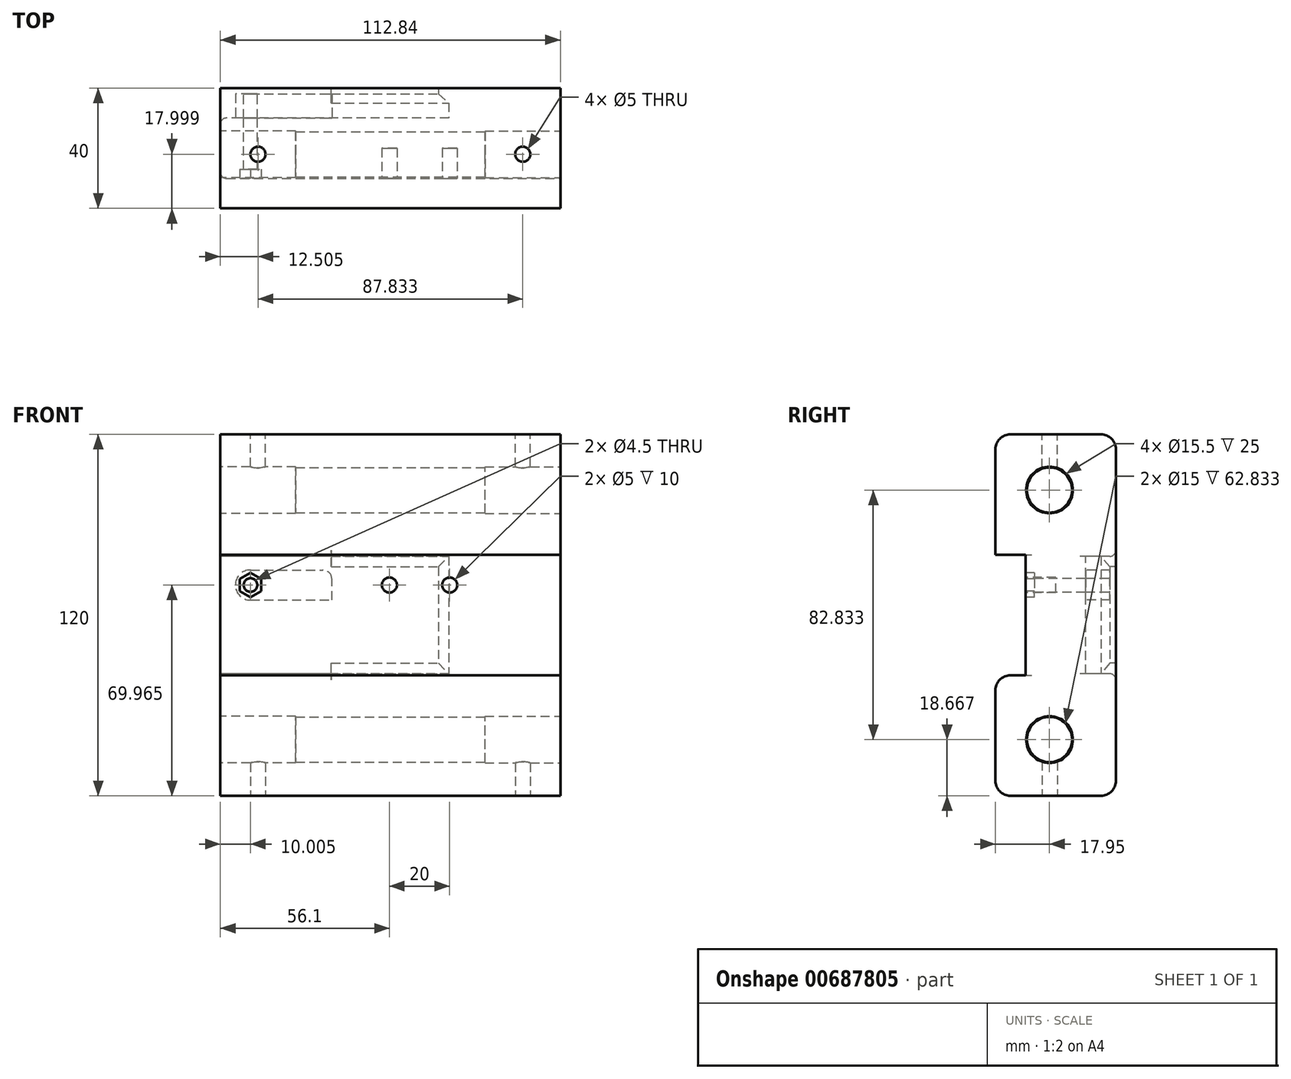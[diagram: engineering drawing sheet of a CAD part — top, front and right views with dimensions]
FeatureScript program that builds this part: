
annotation { "Feature Type Name" : "Feature", "Feature Type Description" : "" }
export const myFeature = defineFeature(function(context is Context, id is Id, definition is map)
    precondition{}
    {
        {
            var Q0;
            Q0=qCreatedBy(makeId("Top.planeOp"),FACE);
            var sketch = newSketch(context, id + "F0", { "sketchPlane" : qUnion([Q0])});
            skLineSegment(sketch, "E0.bottom", {"start": v(-54.1, 12.05) * mm, "end": v(58.73, 12.05) * mm});
            skLineSegment(sketch, "E0.top", {"start": v(-54.1, -17.95) * mm, "end": v(58.73, -17.95) * mm});
            skLineSegment(sketch, "E0.left", {"start": v(-54.1, 12.05) * mm, "end": v(-54.1, -17.95) * mm});
            skLineSegment(sketch, "E0.right", {"start": v(58.73, 12.05) * mm, "end": v(58.73, -17.95) * mm});
            skSolve(sketch);
        }
        {
            var Q0;
            Q0=makeQuery(id+"F0.imprint","IMPRINT",FACE,{"disambiguationData":[TD([[makeQuery(id+"F0.imprint","IMPRINT",EDGE,{"derivedFrom":sQuery(id+"F0.wireOp",EDGE,"E0.bottom")}),-1.0]])]});
            extrude(context, id + "F1", {"entities" : qUnion([Q0]), "depth" : 120 * mm, "offsetDistance" : 25 * mm});
        }
        {
            var Q0;
            Q0=makeQuery(id+"F1.opExtrude","SWEPT_FACE",FACE,{"disambiguationData":[OSD([sQuery(id+"F0.wireOp",EDGE,"E0.bottom")])]});
            var sketch = newSketch(context, id + "F2", { "sketchPlane" : qUnion([Q0])});
            skLineSegment(sketch, "E1.bottom", {"start": v(-21.73, 40.5) * mm, "end": v(17.27, 40.5) * mm});
            skLineSegment(sketch, "E1.top", {"start": v(-21.73, 79.5) * mm, "end": v(17.27, 79.5) * mm});
            skLineSegment(sketch, "E1.left", {"start": v(-21.73, 40.5) * mm, "end": v(-21.73, 79.5) * mm});
            skLineSegment(sketch, "E2.bottom", {"start": v(-18.73, 43.5) * mm, "end": v(14.27, 43.5) * mm});
            skLineSegment(sketch, "E2.top", {"start": v(-18.73, 76.5) * mm, "end": v(14.27, 76.5) * mm});
            skLineSegment(sketch, "E2.left", {"start": v(-18.73, 43.5) * mm, "end": v(-18.73, 76.5) * mm});
            skLineSegment(sketch, "E3.bottom", {"start": v(17.27, 40.5) * mm, "end": v(54.1, 40.5) * mm});
            skLineSegment(sketch, "E3.top", {"start": v(17.27, 79.5) * mm, "end": v(54.1, 79.5) * mm});
            skLineSegment(sketch, "E3.right", {"start": v(54.1, 40.5) * mm, "end": v(54.1, 79.5) * mm});
            skSolve(sketch);
        }
        {
            var Q0;
            Q0=makeQuery(id+"F2.imprint","IMPRINT",FACE,{"disambiguationData":[TD([[makeQuery(id+"F2.imprint","IMPRINT",EDGE,{"derivedFrom":sQuery(id+"F2.wireOp",EDGE,"E1.bottom")}),-1.0]])]});
            extrude(context, id + "F3", {"entities" : qUnion([Q0]), "operationType" : NewBodyOperationType.ADD, "depth" : 10 * mm, "offsetDistance" : 25 * mm});
        }
        {
            var Q0;
            Q0=makeQuery(id+"F3.opExtrude","SWEPT_FACE",FACE,{"disambiguationData":[OSD([sQuery(id+"F2.wireOp",EDGE,"E1.bottom"),sQuery(id+"F2.wireOp",EDGE,"E3.bottom")])]});
            var sketch = newSketch(context, id + "F4", { "sketchPlane" : qUnion([Q0])});
            skLineSegment(sketch, "E4", {"start": v(18.23, 22.05) * mm, "end": v(18.23, 20.05) * mm});
            skLineSegment(sketch, "E5", {"start": v(18.23, 20.05) * mm, "end": v(21.73, 17.05) * mm});
            skLineSegment(sketch, "E6", {"start": v(21.73, 17.05) * mm, "end": v(21.73, 22.05) * mm});
            skLineSegment(sketch, "E7", {"start": v(21.73, 22.05) * mm, "end": v(18.23, 22.05) * mm});
            skSolve(sketch);
        }
        {
            var Q0;
            Q0=makeQuery(id+"F3.opExtrude","SWEPT_FACE",FACE,{"disambiguationData":[OSD([sQuery(id+"F2.wireOp",EDGE,"E1.left")])]});
            var sketch = newSketch(context, id + "F5", { "sketchPlane" : qUnion([Q0])});
            skLineSegment(sketch, "E8", {"start": v(-17.05, 40.5) * mm, "end": v(-20.05, 44) * mm});
            skLineSegment(sketch, "E9", {"start": v(-20.05, 44) * mm, "end": v(-22.05, 44) * mm});
            skLineSegment(sketch, "E10", {"start": v(-22.05, 44) * mm, "end": v(-22.05, 40.5) * mm});
            skLineSegment(sketch, "E11", {"start": v(-22.05, 40.5) * mm, "end": v(-17.05, 40.5) * mm});
            skLineSegment(sketch, "E12", {"start": v(-22.05, 60) * mm, "end": v(-12.05, 60) * mm, "construction": true});
            skLineSegment(sketch, "E13.MirrorCS", {"start": v(-17.05, 79.5) * mm, "end": v(-20.05, 76) * mm});
            skLineSegment(sketch, "E14.MirrorCS", {"start": v(-22.05, 79.5) * mm, "end": v(-17.05, 79.5) * mm});
            skLineSegment(sketch, "E15.MirrorCS", {"start": v(-20.05, 76) * mm, "end": v(-22.05, 76) * mm});
            skLineSegment(sketch, "E16.MirrorCS", {"start": v(-22.05, 76) * mm, "end": v(-22.05, 79.5) * mm});
            skSolve(sketch);
        }
        {
            var Q0;
            Q0=makeQuery(id+"F5.imprint","IMPRINT",FACE,{"disambiguationData":[TD([[makeQuery(id+"F5.imprint","IMPRINT",EDGE,{"derivedFrom":sQuery(id+"F5.wireOp",EDGE,"E8")}),1.0]])]});
            var Q1;
            Q1=makeQuery(id+"F5.imprint","IMPRINT",FACE,{"disambiguationData":[TD([[makeQuery(id+"F5.imprint","IMPRINT",EDGE,{"derivedFrom":sQuery(id+"F5.wireOp",EDGE,"E13.MirrorCS")}),-1.0]])]});
            extrude(context, id + "F6", {"entities" : qUnion([Q0, Q1]), "operationType" : NewBodyOperationType.ADD, "depth" : 39 * mm, "offsetDistance" : 25 * mm});
        }
        {
            var Q0;
            Q0=makeQuery(id+"F4.imprint","IMPRINT",FACE,{"disambiguationData":[TD([[makeQuery(id+"F4.imprint","IMPRINT",EDGE,{"derivedFrom":sQuery(id+"F4.wireOp",EDGE,"E4")}),1.0]])]});
            extrude(context, id + "F7", {"entities" : qUnion([Q0]), "operationType" : NewBodyOperationType.ADD, "depth" : 39 * mm, "offsetDistance" : 25 * mm});
        }
        {
            var Q0;
            {var subQ0=sQuery(id+"F0.wireOp",EDGE,"E0.right");Q0=makeQuery(id+"F3.boolean.opBoolean","MERGE",FACE,{"derivedFrom":[makeQuery(id+"F1.opExtrude","SWEPT_FACE",FACE,{"disambiguationData":[OSD([subQ0])]}),makeQuery(id+"F3.opExtrude","SWEPT_FACE",FACE,{"disambiguationData":[OSD([sQuery(id+"F0.wireOp",EDGE,"E0.bottom"),subQ0])]})]});}
            var sketch = newSketch(context, id + "F8", { "sketchPlane" : qUnion([Q0])});
            skCircle(sketch, "E17", {"center": v(0, 101.5) * mm, "radius": 7.5 * mm});
            skCircle(sketch, "E18", {"center": v(0, 18.67) * mm, "radius": 7.5 * mm});
            skLineSegment(sketch, "E19.bottom", {"start": v(-17.95, 40) * mm, "end": v(-7.95, 40) * mm});
            skLineSegment(sketch, "E19.top", {"start": v(-17.95, 80) * mm, "end": v(-7.95, 80) * mm});
            skLineSegment(sketch, "E19.left", {"start": v(-17.95, 40) * mm, "end": v(-17.95, 80) * mm});
            skLineSegment(sketch, "E19.right", {"start": v(-7.95, 40) * mm, "end": v(-7.95, 80) * mm});
            skSolve(sketch);
        }
        {
            var Q0;
            Q0=makeQuery(id+"F8.imprint","IMPRINT",FACE,{"disambiguationData":[TD([[makeQuery(id+"F8.imprint","IMPRINT",EDGE,{"derivedFrom":sQuery(id+"F8.wireOp",EDGE,"E17")}),1.0]])]});
            var Q1;
            Q1=makeQuery(id+"F8.imprint","IMPRINT",FACE,{"disambiguationData":[TD([[makeQuery(id+"F8.imprint","IMPRINT",EDGE,{"derivedFrom":sQuery(id+"F8.wireOp",EDGE,"E18")}),1.0]])]});
            var Q2;
            Q2=makeQuery(id+"F8.imprint","IMPRINT",FACE,{"disambiguationData":[TD([[makeQuery(id+"F8.imprint","IMPRINT",EDGE,{"derivedFrom":sQuery(id+"F8.wireOp",EDGE,"E19.bottom")}),1.0]])]});
            extrude(context, id + "F9", {"entities" : qUnion([Q0, Q1, Q2]), "operationType" : NewBodyOperationType.REMOVE, "oppositeDirection" : true, "depth" : 120 * mm, "offsetDistance" : 25 * mm});
        }
        {
            var Q0;
            Q0=makeQuery(id+"F1.opExtrude","SWEPT_FACE",FACE,{"disambiguationData":[OSD([sQuery(id+"F0.wireOp",EDGE,"E0.bottom")])]});
            var sketch = newSketch(context, id + "F10", { "sketchPlane" : qUnion([Q0])});
            skArc(sketch, "E20", {"start": v(44.1, 64.96) * mm, "mid": v(49.1, 69.96) * mm, "end": v(44.1, 74.96) * mm});
            skLineSegment(sketch, "E21.bottom", {"start": v(44.1, 64.96) * mm, "end": v(17.1, 64.96) * mm});
            skLineSegment(sketch, "E21.top", {"start": v(44.1, 74.96) * mm, "end": v(20.1, 74.96) * mm});
            skLineSegment(sketch, "E21.right", {"start": v(17.1, 64.96) * mm, "end": v(17.1, 71.96) * mm});
            skPoint(sketch, "E22.visualSharp", {"position": v(17.1, 74.96) * mm});
            skArc(sketch, "E22.filletArc", {"start": v(20.1, 74.96) * mm, "mid": v(17.98, 74.09) * mm, "end": v(17.1, 71.96) * mm});
            skSolve(sketch);
        }
        {
            var Q0;
            Q0=makeQuery(id+"F10.imprint","IMPRINT",FACE,{"disambiguationData":[TD([[makeQuery(id+"F10.imprint","IMPRINT",EDGE,{"derivedFrom":sQuery(id+"F10.wireOp",EDGE,"E20")}),1.0]])]});
            extrude(context, id + "F11", {"entities" : qUnion([Q0]), "depth" : 8 * mm, "offsetDistance" : 25 * mm});
        }
        {
            var Q0;
            Q0=makeQuery(id+"F11.opExtrude","CAP_FACE",FACE,{"disambiguationData":[OSD([sQuery(id+"F10.wireOp",EDGE,"E20"),sQuery(id+"F10.wireOp",EDGE,"E21.bottom"),sQuery(id+"F10.wireOp",EDGE,"E21.top"),sQuery(id+"F10.wireOp",EDGE,"E21.right"),sQuery(id+"F10.wireOp",EDGE,"E22.filletArc")])],"isStart":false});
            var sketch = newSketch(context, id + "F12", { "sketchPlane" : qUnion([Q0])});
            skCircle(sketch, "E23", {"center": v(44.1, 69.96) * mm, "radius": 2.25 * mm});
            skSolve(sketch);
        }
        {
            var Q0;
            Q0=makeQuery(id+"F12.imprint","IMPRINT",FACE,{"disambiguationData":[TD([[makeQuery(id+"F12.imprint","IMPRINT",EDGE,{"derivedFrom":sQuery(id+"F12.wireOp",EDGE,"E23")}),1.0]])]});
            extrude(context, id + "F13", {"entities" : qUnion([Q0]), "operationType" : NewBodyOperationType.REMOVE, "oppositeDirection" : true, "depth" : 50 * mm, "offsetDistance" : 25 * mm});
        }
        {
            var Q0;
            Q0=makeQuery(id+"F9.boolean.opBoolean","COPY",FACE,{"derivedFrom":makeQuery(id+"F9.opExtrude","SWEPT_FACE",FACE,{"disambiguationData":[OSD([sQuery(id+"F8.wireOp",EDGE,"E19.right")])]})});
            var sketch = newSketch(context, id + "F14", { "sketchPlane" : qUnion([Q0])});
            skCircle(sketch, "E24.cCircle", {"center": v(-44.1, 69.96) * mm, "radius": 3.5 * mm, "construction": true});
            skLineSegment(sketch, "E24.0", {"start": v(-40.6, 71.99) * mm, "end": v(-40.6, 67.94) * mm});
            skLineSegment(sketch, "E24.1", {"start": v(-40.6, 67.94) * mm, "end": v(-44.1, 65.92) * mm});
            skLineSegment(sketch, "E24.2", {"start": v(-44.1, 65.92) * mm, "end": v(-47.6, 67.94) * mm});
            skLineSegment(sketch, "E24.3", {"start": v(-47.6, 67.94) * mm, "end": v(-47.6, 71.99) * mm});
            skLineSegment(sketch, "E24.4", {"start": v(-47.6, 71.99) * mm, "end": v(-44.1, 74) * mm});
            skLineSegment(sketch, "E24.5", {"start": v(-44.1, 74) * mm, "end": v(-40.6, 71.99) * mm});
            skPoint(sketch, "E24.0.midPoint", {"position": v(-40.6, 69.96) * mm});
            skCircle(sketch, "E25", {"center": v(1.99, 69.96) * mm, "radius": 2.5 * mm});
            skCircle(sketch, "E26", {"center": v(21.99, 69.96) * mm, "radius": 2.5 * mm});
            skSolve(sketch);
        }
        {
            var Q0;
            Q0=makeQuery(id+"F14.imprint","IMPRINT",FACE,{"disambiguationData":[TD([[makeQuery(id+"F14.imprint","IMPRINT",EDGE,{"derivedFrom":sQuery(id+"F14.wireOp",EDGE,"E24.0")}),-1.0]])]});
            extrude(context, id + "F15", {"entities" : qUnion([Q0]), "operationType" : NewBodyOperationType.REMOVE, "oppositeDirection" : true, "depth" : 3 * mm, "offsetDistance" : 25 * mm});
        }
        {
            var Q0;
            Q0=makeQuery(id+"F9.boolean.opBoolean","COPY",EDGE,{"derivedFrom":makeQuery(id+"F9.opExtrude","SWEPT_EDGE",EDGE,{"disambiguationData":[OSD([sQuery(id+"F0.wireOp",EDGE,"E0.top"),sQuery(id+"F0.wireOp",EDGE,"E0.right"),sQuery(id+"F8.wireOp",EDGE,"E19.bottom"),sQuery(id+"F8.wireOp",EDGE,"E19.left")])]})});
            var Q1;
            Q1=makeQuery(id+"F9.boolean.opBoolean","COPY",EDGE,{"derivedFrom":makeQuery(id+"F9.opExtrude","SWEPT_EDGE",EDGE,{"disambiguationData":[OSD([sQuery(id+"F0.wireOp",EDGE,"E0.top"),sQuery(id+"F0.wireOp",EDGE,"E0.right"),sQuery(id+"F8.wireOp",EDGE,"E19.top"),sQuery(id+"F8.wireOp",EDGE,"E19.left")])]})});
            var Q2;
            Q2=makeQuery(id+"F1.opExtrude","CAP_EDGE",EDGE,{"disambiguationData":[OSD([sQuery(id+"F0.wireOp",EDGE,"E0.top")])],"isStart":false});
            var Q3;
            {var subQ0=sQuery(id+"F0.wireOp",EDGE,"E0.bottom");Q3=makeQuery(id+"F3.opExtrude","CAP_EDGE",EDGE,{"disambiguationData":[OSD([subQ0]),TDD([makeQuery(id+"F2.imprint","IMPRINT",EDGE,{"derivedFrom":makeQuery(id+"F1.opExtrude","CAP_EDGE",EDGE,{"disambiguationData":[OSD([subQ0])],"isStart":false})})])],"isStart":false});}
            var Q4;
            Q4=makeQuery(id+"F1.opExtrude","CAP_EDGE",EDGE,{"disambiguationData":[OSD([sQuery(id+"F0.wireOp",EDGE,"E0.top")])],"isStart":true});
            var Q5;
            {var subQ0=sQuery(id+"F0.wireOp",EDGE,"E0.bottom");Q5=makeQuery(id+"F3.opExtrude","CAP_EDGE",EDGE,{"disambiguationData":[OSD([subQ0]),TDD([makeQuery(id+"F2.imprint","IMPRINT",EDGE,{"derivedFrom":makeQuery(id+"F1.opExtrude","CAP_EDGE",EDGE,{"disambiguationData":[OSD([subQ0])],"isStart":true})})])],"isStart":false});}
            fillet(context, id + "F16", {"entities" : qUnion([Q0, Q1, Q2, Q3, Q4, Q5]), "radius" : 5 * mm, "tangentPropagation" : true, "allowEdgeOverflow" : false});
        }
        {
            var Q0;
            Q0=makeQuery(id+"F3.opExtrude","CAP_EDGE",EDGE,{"disambiguationData":[OSD([sQuery(id+"F2.wireOp",EDGE,"E1.top"),sQuery(id+"F2.wireOp",EDGE,"E3.top")])],"isStart":false});
            var Q1;
            Q1=makeQuery(id+"F3.opExtrude","CAP_EDGE",EDGE,{"disambiguationData":[OSD([sQuery(id+"F2.wireOp",EDGE,"E1.bottom"),sQuery(id+"F2.wireOp",EDGE,"E3.bottom")])],"isStart":false});
            var Q2;
            Q2=makeQuery(id+"F1.opExtrude","SWEPT_EDGE",EDGE,{"disambiguationData":[OSD([sQuery(id+"F0.wireOp",EDGE,"E0.bottom"),sQuery(id+"F0.wireOp",EDGE,"E0.left")])]});
            var Q3;
            {var subQ0=sQuery(id+"F0.wireOp",EDGE,"E0.bottom");var subQ1=sQuery(id+"F0.wireOp",EDGE,"E0.left");var subQ2=makeQuery(id+"F1.opExtrude","SWEPT_EDGE",EDGE,{"disambiguationData":[OSD([subQ0,subQ1])]});Q3=makeQuery(id+"F9.boolean.opBoolean","INTERSECT",EDGE,{"derivedFrom":[makeQuery(id+"F3.boolean.opBoolean","MERGE",FACE,{"derivedFrom":[makeQuery(id+"F1.opExtrude","SWEPT_FACE",FACE,{"disambiguationData":[OSD([subQ1])]}),makeQuery(id+"F3.opExtrude","SWEPT_FACE",FACE,{"disambiguationData":[OSD([subQ0,subQ1]),TDD([makeQuery(id+"F2.imprint","IMPRINT",EDGE,{"disambiguationData":[TD([[makeQuery(id+"F2.imprint","INTERSECT",VERTEX,{"derivedFrom":[subQ2,makeQuery(id+"F1.opExtrude","CAP_EDGE",EDGE,{"disambiguationData":[OSD([subQ0])],"isStart":true})]}),1.0]])],"derivedFrom":subQ2})])]}),makeQuery(id+"F3.opExtrude","SWEPT_FACE",FACE,{"disambiguationData":[OSD([subQ0,subQ1]),TDD([makeQuery(id+"F2.imprint","IMPRINT",EDGE,{"disambiguationData":[TD([[makeQuery(id+"F2.imprint","INTERSECT",VERTEX,{"derivedFrom":[subQ2,makeQuery(id+"F1.opExtrude","CAP_EDGE",EDGE,{"disambiguationData":[OSD([subQ0])],"isStart":false})]}),-1.0]])],"derivedFrom":subQ2})])]})]}),makeQuery(id+"F9.opExtrude","SWEPT_FACE",FACE,{"disambiguationData":[OSD([sQuery(id+"F8.wireOp",EDGE,"E19.right")])]})]});}
            var Q4;
            Q4=makeQuery(id+"F9.boolean.opBoolean","COPY",EDGE,{"derivedFrom":makeQuery(id+"F9.opExtrude","CAP_EDGE",EDGE,{"disambiguationData":[OSD([sQuery(id+"F8.wireOp",EDGE,"E19.right")])],"isStart":true})});
            fillet(context, id + "F17", {"entities" : qUnion([Q0, Q1, Q2, Q3, Q4]), "radius" : 2 * mm, "tangentPropagation" : true, "allowEdgeOverflow" : false});
        }
        {
            var Q0;
            Q0=makeQuery(id+"F14.imprint","IMPRINT",FACE,{"disambiguationData":[TD([[makeQuery(id+"F14.imprint","IMPRINT",EDGE,{"derivedFrom":sQuery(id+"F14.wireOp",EDGE,"E25")}),1.0]])]});
            var Q1;
            Q1=makeQuery(id+"F14.imprint","IMPRINT",FACE,{"disambiguationData":[TD([[makeQuery(id+"F14.imprint","IMPRINT",EDGE,{"derivedFrom":sQuery(id+"F14.wireOp",EDGE,"E26")}),1.0]])]});
            extrude(context, id + "F18", {"entities" : qUnion([Q0, Q1]), "operationType" : NewBodyOperationType.REMOVE, "oppositeDirection" : true, "depth" : 10 * mm, "offsetDistance" : 25 * mm});
        }
        {
            var Q0;
            {var subQ0=sQuery(id+"F0.wireOp",EDGE,"E0.right");Q0=makeQuery(id+"F3.boolean.opBoolean","MERGE",FACE,{"derivedFrom":[makeQuery(id+"F1.opExtrude","SWEPT_FACE",FACE,{"disambiguationData":[OSD([subQ0])]}),makeQuery(id+"F3.opExtrude","SWEPT_FACE",FACE,{"disambiguationData":[OSD([sQuery(id+"F0.wireOp",EDGE,"E0.bottom"),subQ0])]})]});}
            var sketch = newSketch(context, id + "F19", { "sketchPlane" : qUnion([Q0])});
            skCircle(sketch, "E27", {"center": v(0, 101.5) * mm, "radius": 7.75 * mm});
            skCircle(sketch, "E28", {"center": v(0, 18.67) * mm, "radius": 7.75 * mm});
            skSolve(sketch);
        }
        {
            var Q0;
            Q0=makeQuery(id+"F19.imprint","IMPRINT",FACE,{"disambiguationData":[TD([[makeQuery(id+"F19.imprint","IMPRINT",EDGE,{"derivedFrom":sQuery(id+"F19.wireOp",EDGE,"E27")}),1.0]])]});
            var Q1;
            Q1=makeQuery(id+"F19.imprint","IMPRINT",FACE,{"disambiguationData":[TD([[makeQuery(id+"F19.imprint","IMPRINT",EDGE,{"derivedFrom":sQuery(id+"F19.wireOp",EDGE,"E28")}),1.0]])]});
            extrude(context, id + "F20", {"entities" : qUnion([Q0, Q1]), "operationType" : NewBodyOperationType.REMOVE, "oppositeDirection" : true, "depth" : 25 * mm, "offsetDistance" : 25 * mm});
        }
        {
            var Q0;
            {var subQ0=sQuery(id+"F0.wireOp",EDGE,"E0.bottom");var subQ1=sQuery(id+"F0.wireOp",EDGE,"E0.left");var subQ2=makeQuery(id+"F1.opExtrude","SWEPT_EDGE",EDGE,{"disambiguationData":[OSD([subQ0,subQ1])]});Q0=makeQuery(id+"F3.boolean.opBoolean","MERGE",FACE,{"derivedFrom":[makeQuery(id+"F1.opExtrude","SWEPT_FACE",FACE,{"disambiguationData":[OSD([subQ1])]}),makeQuery(id+"F3.opExtrude","SWEPT_FACE",FACE,{"disambiguationData":[OSD([subQ0,subQ1]),TDD([makeQuery(id+"F2.imprint","IMPRINT",EDGE,{"disambiguationData":[TD([[makeQuery(id+"F2.imprint","INTERSECT",VERTEX,{"derivedFrom":[subQ2,makeQuery(id+"F1.opExtrude","CAP_EDGE",EDGE,{"disambiguationData":[OSD([subQ0])],"isStart":true})]}),1.0]])],"derivedFrom":subQ2})])]}),makeQuery(id+"F3.opExtrude","SWEPT_FACE",FACE,{"disambiguationData":[OSD([subQ0,subQ1]),TDD([makeQuery(id+"F2.imprint","IMPRINT",EDGE,{"disambiguationData":[TD([[makeQuery(id+"F2.imprint","INTERSECT",VERTEX,{"derivedFrom":[subQ2,makeQuery(id+"F1.opExtrude","CAP_EDGE",EDGE,{"disambiguationData":[OSD([subQ0])],"isStart":false})]}),-1.0]])],"derivedFrom":subQ2})])]})]});}
            var sketch = newSketch(context, id + "F21", { "sketchPlane" : qUnion([Q0])});
            skCircle(sketch, "E29", {"center": v(0, 101.5) * mm, "radius": 7.75 * mm});
            skCircle(sketch, "E30", {"center": v(0, 18.67) * mm, "radius": 7.75 * mm});
            skSolve(sketch);
        }
        {
            var Q0;
            Q0=makeQuery(id+"F21.imprint","IMPRINT",FACE,{"disambiguationData":[TD([[makeQuery(id+"F21.imprint","IMPRINT",EDGE,{"derivedFrom":sQuery(id+"F21.wireOp",EDGE,"E29")}),1.0]])]});
            var Q1;
            Q1=makeQuery(id+"F21.imprint","IMPRINT",FACE,{"disambiguationData":[TD([[makeQuery(id+"F21.imprint","IMPRINT",EDGE,{"derivedFrom":sQuery(id+"F21.wireOp",EDGE,"E30")}),1.0]])]});
            extrude(context, id + "F22", {"entities" : qUnion([Q0, Q1]), "operationType" : NewBodyOperationType.REMOVE, "oppositeDirection" : true, "depth" : 25 * mm, "offsetDistance" : 25 * mm});
        }
        {
            var Q0;
            {var subQ0=sQuery(id+"F0.wireOp",EDGE,"E0.bottom");Q0=makeQuery(id+"F3.boolean.opBoolean","MERGE",FACE,{"derivedFrom":[makeQuery(id+"F1.opExtrude","CAP_FACE",FACE,{"disambiguationData":[OSD([subQ0,sQuery(id+"F0.wireOp",EDGE,"E0.top"),sQuery(id+"F0.wireOp",EDGE,"E0.left"),sQuery(id+"F0.wireOp",EDGE,"E0.right")])],"isStart":true}),makeQuery(id+"F3.opExtrude","SWEPT_FACE",FACE,{"disambiguationData":[OSD([subQ0]),TDD([makeQuery(id+"F2.imprint","IMPRINT",EDGE,{"derivedFrom":makeQuery(id+"F1.opExtrude","CAP_EDGE",EDGE,{"disambiguationData":[OSD([subQ0])],"isStart":true})})])]})]});}
            var sketch = newSketch(context, id + "F23", { "sketchPlane" : qUnion([Q0])});
            skCircle(sketch, "E31", {"center": v(-41.6, -0.05) * mm, "radius": 2.5 * mm});
            skPoint(sketch, "E31.centerSnap0", {"position": v(-54.1, -0.05) * mm});
            skCircle(sketch, "E32", {"center": v(46.23, -0.05) * mm, "radius": 2.5 * mm});
            skPoint(sketch, "E32.centerSnap0", {"position": v(58.73, -0.05) * mm});
            skSolve(sketch);
        }
        {
            var Q0;
            {var subQ0=sQuery(id+"F0.wireOp",EDGE,"E0.bottom");Q0=makeQuery(id+"F3.boolean.opBoolean","MERGE",FACE,{"derivedFrom":[makeQuery(id+"F1.opExtrude","CAP_FACE",FACE,{"disambiguationData":[OSD([subQ0,sQuery(id+"F0.wireOp",EDGE,"E0.top"),sQuery(id+"F0.wireOp",EDGE,"E0.left"),sQuery(id+"F0.wireOp",EDGE,"E0.right")])],"isStart":false}),makeQuery(id+"F3.opExtrude","SWEPT_FACE",FACE,{"disambiguationData":[OSD([subQ0]),TDD([makeQuery(id+"F2.imprint","IMPRINT",EDGE,{"derivedFrom":makeQuery(id+"F1.opExtrude","CAP_EDGE",EDGE,{"disambiguationData":[OSD([subQ0])],"isStart":false})})])]})]});}
            var sketch = newSketch(context, id + "F24", { "sketchPlane" : qUnion([Q0])});
            skCircle(sketch, "E33", {"center": v(-41.6, 0.05) * mm, "radius": 2.5 * mm});
            skPoint(sketch, "E33.centerSnap0", {"position": v(-54.1, 0.05) * mm});
            skCircle(sketch, "E34", {"center": v(46.23, 0.05) * mm, "radius": 2.5 * mm});
            skPoint(sketch, "E34.centerSnap0", {"position": v(58.73, 0.05) * mm});
            skSolve(sketch);
        }
        {
            var Q0;
            Q0=makeQuery(id+"F24.imprint","IMPRINT",FACE,{"disambiguationData":[TD([[makeQuery(id+"F24.imprint","IMPRINT",EDGE,{"derivedFrom":sQuery(id+"F24.wireOp",EDGE,"E33")}),1.0]])]});
            var Q1;
            Q1=makeQuery(id+"F23.imprint","IMPRINT",FACE,{"disambiguationData":[TD([[makeQuery(id+"F23.imprint","IMPRINT",EDGE,{"derivedFrom":sQuery(id+"F23.wireOp",EDGE,"E31")}),1.0]])]});
            var Q2;
            Q2=makeQuery(id+"F24.imprint","IMPRINT",FACE,{"disambiguationData":[TD([[makeQuery(id+"F24.imprint","IMPRINT",EDGE,{"derivedFrom":sQuery(id+"F24.wireOp",EDGE,"E34")}),1.0]])]});
            var Q3;
            Q3=makeQuery(id+"F23.imprint","IMPRINT",FACE,{"disambiguationData":[TD([[makeQuery(id+"F23.imprint","IMPRINT",EDGE,{"derivedFrom":sQuery(id+"F23.wireOp",EDGE,"E32")}),1.0]])]});
            extrude(context, id + "F25", {"entities" : qUnion([Q0, Q1, Q2, Q3]), "operationType" : NewBodyOperationType.REMOVE, "oppositeDirection" : true, "depth" : 13.1 * mm, "offsetDistance" : 25 * mm});
        }
        {
            var Q0;
            Q0=makeQuery(id+"F23.imprint","IMPRINT",FACE,{"disambiguationData":[TD([[makeQuery(id+"F23.imprint","IMPRINT",EDGE,{"derivedFrom":sQuery(id+"F23.wireOp",EDGE,"E31")}),1.0]])]});
            var Q1;
            Q1=makeQuery(id+"F23.imprint","IMPRINT",FACE,{"disambiguationData":[TD([[makeQuery(id+"F23.imprint","IMPRINT",EDGE,{"derivedFrom":sQuery(id+"F23.wireOp",EDGE,"E32")}),1.0]])]});
            extrude(context, id + "F26", {"entities" : qUnion([Q0, Q1]), "operationType" : NewBodyOperationType.REMOVE, "oppositeDirection" : true, "depth" : 25 * mm, "offsetDistance" : 25 * mm});
        }
    });
